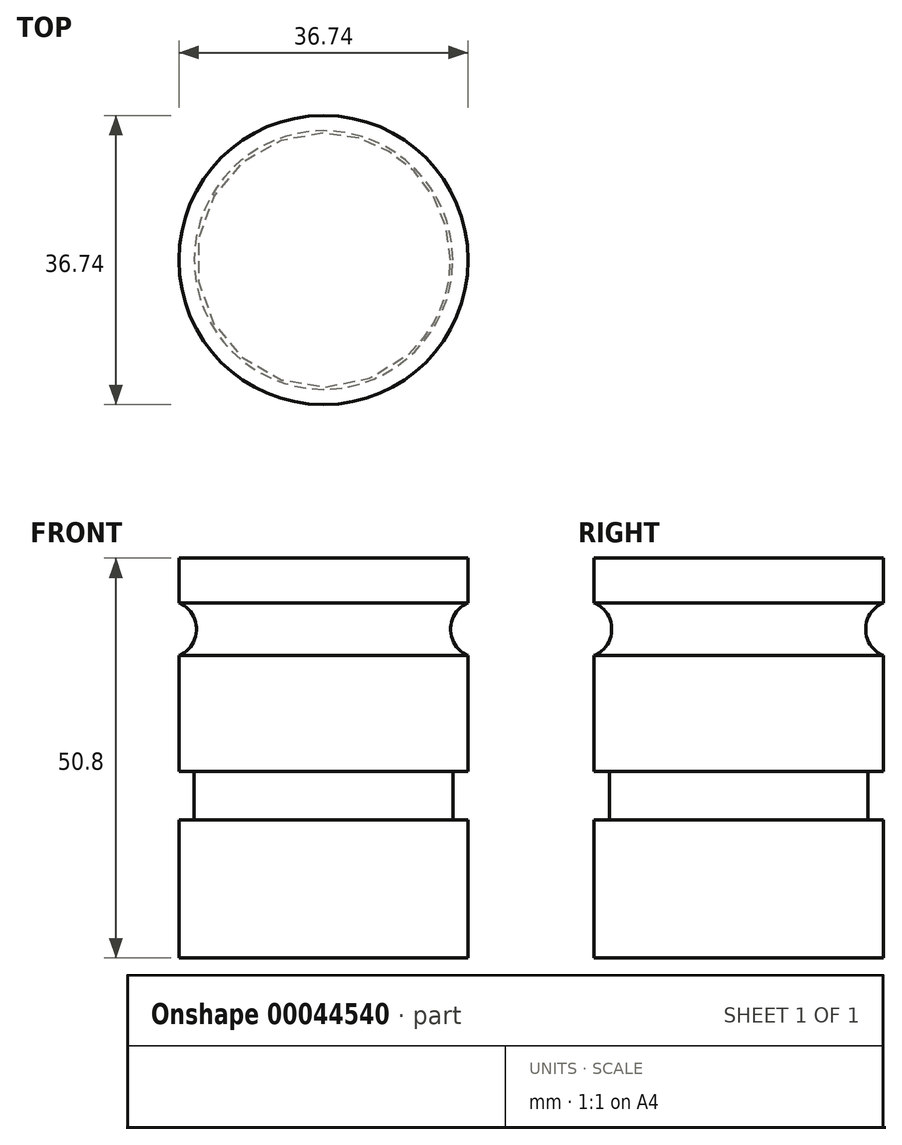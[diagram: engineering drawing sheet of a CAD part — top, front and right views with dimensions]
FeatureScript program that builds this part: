
annotation { "Feature Type Name" : "Feature", "Feature Type Description" : "" }
export const myFeature = defineFeature(function(context is Context, id is Id, definition is map)
    precondition{}
    {
        {
            var Q0;
            Q0=qCreatedBy(makeId("Top.planeOp"),FACE);
            var sketch = newSketch(context, id + "F0", { "sketchPlane" : qUnion([Q0])});
            skCircle(sketch, "E0", {"center": v(0, 0) * mm, "radius": 18.37 * mm});
            skSolve(sketch);
        }
        {
            var Q0;
            Q0 = qSketchRegion(id + "F0", true);
            extrude(context, id + "F1", {"entities" : qUnion([Q0]), "depth" : 50.8 * mm});
        }
        {
            var Q0;
            Q0=qCreatedBy(makeId("Right.planeOp"),FACE);
            var sketch = newSketch(context, id + "F2", { "sketchPlane" : qUnion([Q0])});
            skCircle(sketch, "E1", {"center": v(-19.74, 41.79) * mm, "radius": 3.62 * mm});
            skLineSegment(sketch, "E2.rect.bottom", {"start": v(-16.42, 17.57) * mm, "end": v(-23.06, 17.57) * mm});
            skLineSegment(sketch, "E2.rect.top", {"start": v(-16.42, 23.7) * mm, "end": v(-23.06, 23.7) * mm});
            skLineSegment(sketch, "E2.rect.left", {"start": v(-16.42, 17.57) * mm, "end": v(-16.42, 23.7) * mm});
            skLineSegment(sketch, "E2.rect.right", {"start": v(-23.06, 17.57) * mm, "end": v(-23.06, 23.7) * mm});
            skPoint(sketch, "E2.rect.middle", {"position": v(-19.74, 20.64) * mm});
            skLineSegment(sketch, "E3", {"start": v(0, -9.89) * mm, "end": v(0, 57.42) * mm, "construction": true});
            skSolve(sketch);
        }
        {
            var Q0;
            Q0 = qSketchRegion(id + "F2", true);
            var Q1;
            Q1=sQuery(id+"F2.wireOp",EDGE,"E3");
            revolve(context, id + "F3", {"operationType" : NewBodyOperationType.REMOVE, "entities" : qUnion([Q0]), "axis" : qUnion([Q1]), "revolveType" : RevolveType.FULL, "oppositeDirection" : true});
        }
    });
